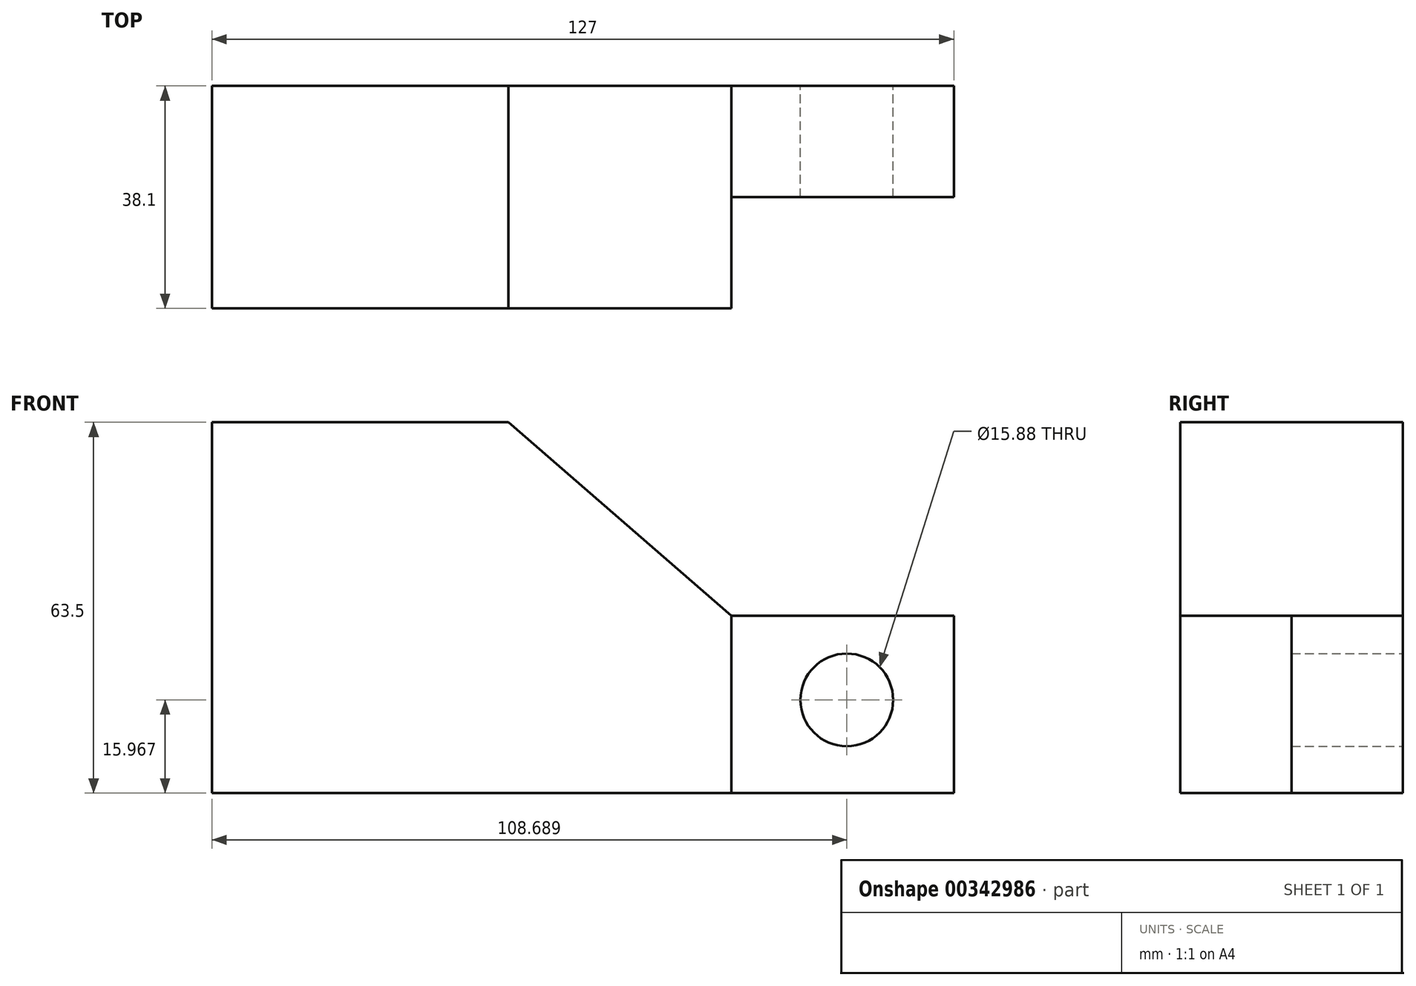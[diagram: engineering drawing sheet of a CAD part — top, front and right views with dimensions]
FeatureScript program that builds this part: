
annotation { "Feature Type Name" : "Feature", "Feature Type Description" : "" }
export const myFeature = defineFeature(function(context is Context, id is Id, definition is map)
    precondition{}
    {
        {
            var Q0;
            Q0=qCreatedBy(makeId("Front.planeOp"),FACE);
            var sketch = newSketch(context, id + "F0", { "sketchPlane" : qUnion([Q0])});
            skLineSegment(sketch, "E0", {"start": v(-65.97, -30.37) * mm, "end": v(61.03, -30.37) * mm});
            skLineSegment(sketch, "E1", {"start": v(-65.97, -30.37) * mm, "end": v(-65.97, 33.13) * mm});
            skLineSegment(sketch, "E2", {"start": v(61.03, -30.37) * mm, "end": v(61.03, 0) * mm});
            skLineSegment(sketch, "E3", {"start": v(61.03, 0) * mm, "end": v(22.93, 0) * mm});
            skLineSegment(sketch, "E4", {"start": v(-65.97, 33.13) * mm, "end": v(-15.17, 33.13) * mm});
            skLineSegment(sketch, "E5", {"start": v(-15.17, 33.13) * mm, "end": v(22.93, 0) * mm});
            skLineSegment(sketch, "E6", {"start": v(22.93, 0) * mm, "end": v(22.93, -30.37) * mm});
            skCircle(sketch, "E7", {"center": v(42.72, -14.4) * mm, "radius": 7.94 * mm});
            skSolve(sketch);
        }
        {
            var Q0;
            {var subQ0=sQuery(id+"F0.wireOp",EDGE,"E1");Q0=makeQuery(id+"F0.imprint","IMPRINT",FACE,{"disambiguationData":[TD([[makeQuery(id+"F0.imprint","IMPRINT",EDGE,{"derivedFrom":subQ0}),-1.0]])]});}
            extrude(context, id + "F1", {"entities" : qUnion([Q0]), "depth" : 38.1 * mm});
        }
        {
            var Q0;
            {var subQ1=sQuery(id+"F0.wireOp",EDGE,"E2");Q0=makeQuery(id+"F0.imprint","IMPRINT",FACE,{"disambiguationData":[TD([[makeQuery(id+"F0.imprint","IMPRINT",EDGE,{"derivedFrom":subQ1}),1.0]])]});}
            extrude(context, id + "F2", {"entities" : qUnion([Q0]), "operationType" : NewBodyOperationType.ADD, "depth" : 19.05 * mm});
        }
    });
